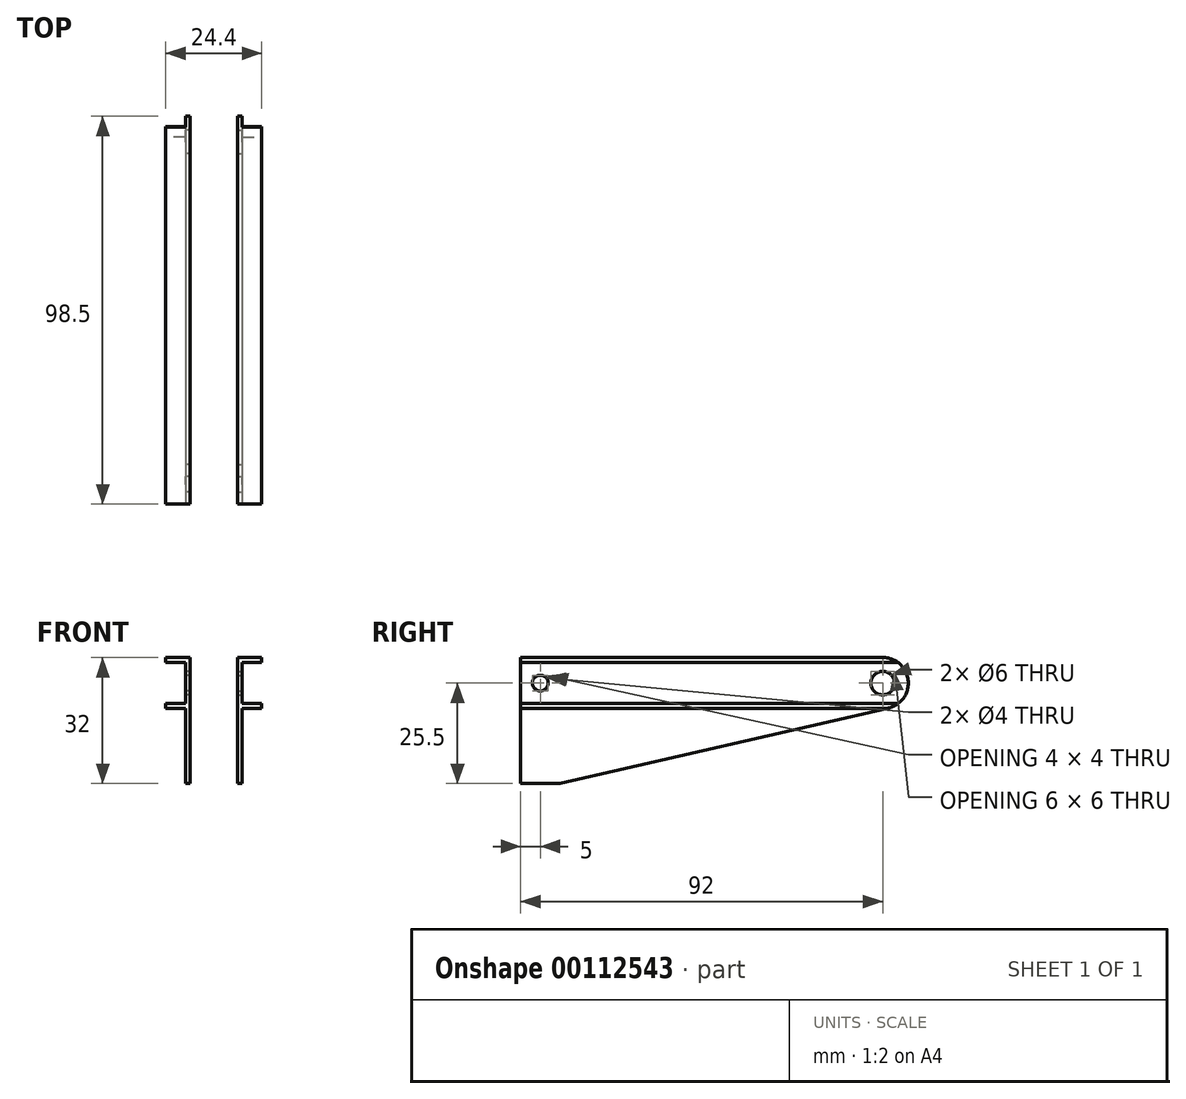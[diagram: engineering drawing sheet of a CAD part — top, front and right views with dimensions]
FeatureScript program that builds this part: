
annotation { "Feature Type Name" : "Feature", "Feature Type Description" : "" }
export const myFeature = defineFeature(function(context is Context, id is Id, definition is map)
    precondition{}
    {
        {
            var Q0;
            Q0=qCreatedBy(makeId("Front.planeOp"),FACE);
            var sketch = newSketch(context, id + "F0", { "sketchPlane" : qUnion([Q0])});
            skLineSegment(sketch, "E0", {"start": v(0, 0) * mm, "end": v(0, 16) * mm});
            skLineSegment(sketch, "E1", {"start": v(0, 16) * mm, "end": v(1.2, 16) * mm});
            skLineSegment(sketch, "E2", {"start": v(1.2, 16) * mm, "end": v(1.2, 16) * mm});
            skLineSegment(sketch, "E3", {"start": v(1.2, 16) * mm, "end": v(6.2, 16) * mm});
            skLineSegment(sketch, "E4", {"start": v(6.2, 16) * mm, "end": v(6.2, 14.8) * mm});
            skLineSegment(sketch, "E5", {"start": v(6.2, 14.8) * mm, "end": v(1.2, 14.8) * mm});
            skLineSegment(sketch, "E6", {"start": v(1.2, 14.8) * mm, "end": v(1.2, 4.3) * mm});
            skLineSegment(sketch, "E7", {"start": v(1.2, 4.3) * mm, "end": v(6.2, 4.3) * mm});
            skLineSegment(sketch, "E8", {"start": v(6.2, 4.3) * mm, "end": v(6.2, 3.1) * mm});
            skLineSegment(sketch, "E9", {"start": v(6.2, 3.1) * mm, "end": v(1.2, 3.1) * mm});
            skLineSegment(sketch, "E10", {"start": v(0, 0) * mm, "end": v(0, -16) * mm});
            skLineSegment(sketch, "E11", {"start": v(0, -16) * mm, "end": v(1.2, -16) * mm});
            skLineSegment(sketch, "E12", {"start": v(1.2, -16) * mm, "end": v(1.2, 3.1) * mm});
            skSolve(sketch);
        }
        {
            var Q0;
            Q0=makeQuery(id+"F0.imprint","IMPRINT",FACE,{"disambiguationData":[TD([[makeQuery(id+"F0.imprint","IMPRINT",EDGE,{"derivedFrom":sQuery(id+"F0.wireOp",EDGE,"E0")}),-1.0]])]});
            extrude(context, id + "F1", {"entities" : qUnion([Q0]), "oppositeDirection" : true, "depth" : 100 * mm});
        }
        {
            var Q0;
            Q0=makeQuery(id+"F1.opExtrude","SWEPT_FACE",FACE,{"disambiguationData":[OSD([sQuery(id+"F0.wireOp",EDGE,"E2")])]});
            var Q1;
            Q1=makeQuery(id+"F1.opExtrude","SWEPT_FACE",FACE,{"disambiguationData":[OSD([sQuery(id+"F0.wireOp",EDGE,"E6")])]});
            cPlane(context, id + "F2", {"entities" : qUnion([Q0, Q1]), "cplaneType" : CPlaneType.OFFSET, "offset" : 0 * mm, "width" : 150 * mm, "height" : 150 * mm});
        }
        {
            var Q0;
            Q0=qCreatedBy(id+"F2.planeOp",FACE);
            var sketch = newSketch(context, id + "F3", { "sketchPlane" : qUnion([Q0])});
            skCircle(sketch, "E13", {"center": v(5, 9.5) * mm, "radius": 2 * mm});
            skCircle(sketch, "E14.MirrorC", {"center": v(5, -10.5) * mm, "radius": 2 * mm});
            skLineSegment(sketch, "E15", {"start": v(100, 16) * mm, "end": v(100, 16) * mm});
            skCircle(sketch, "E16", {"center": v(5, 9.5) * mm, "radius": 5 * mm});
            skCircle(sketch, "E17", {"center": v(92, 9.5) * mm, "radius": 3 * mm});
            skLineSegment(sketch, "E18", {"start": v(93.45, 3.16) * mm, "end": v(10, -16) * mm});
            skArc(sketch, "E19", {"start": v(93.45, 3.16) * mm, "mid": v(98.46, 10.23) * mm, "end": v(92, 16) * mm});
            skLineSegment(sketch, "E20", {"start": v(92, 16) * mm, "end": v(100, 16) * mm});
            skLineSegment(sketch, "E21", {"start": v(100, 16) * mm, "end": v(100, -16) * mm});
            skLineSegment(sketch, "E22", {"start": v(100, -16) * mm, "end": v(10, -16) * mm});
            skSolve(sketch);
        }
        {
            var Q0;
            Q0=makeQuery(id+"F3.imprint","IMPRINT",FACE,{"disambiguationData":[TD([[makeQuery(id+"F3.imprint","IMPRINT",EDGE,{"derivedFrom":sQuery(id+"F3.wireOp",EDGE,"E14.MirrorC")}),-1.0]])]});
            var Q1;
            Q1=makeQuery(id+"F3.imprint","IMPRINT",FACE,{"disambiguationData":[TD([[makeQuery(id+"F3.imprint","IMPRINT",EDGE,{"derivedFrom":sQuery(id+"F3.wireOp",EDGE,"E13")}),1.0]])]});
            var Q2;
            Q2=makeQuery(id+"F3.imprint","IMPRINT",FACE,{"disambiguationData":[TD([[makeQuery(id+"F3.imprint","IMPRINT",EDGE,{"derivedFrom":sQuery(id+"F3.wireOp",EDGE,"574HhtLP-nTTJ-pekG-s0HU-Gk7TssawcMeE")}),-1.0]])]});
            var Q3;
            Q3=makeQuery(id+"F3.imprint","IMPRINT",FACE,{"disambiguationData":[TD([[makeQuery(id+"F3.imprint","IMPRINT",EDGE,{"derivedFrom":sQuery(id+"F3.wireOp",EDGE,"buxoA0jU-tP47-w18K-Fbsk-EydC5CnxEHID")}),1.0]])]});
            var Q4;
            Q4=makeQuery(id+"F3.imprint","IMPRINT",FACE,{"disambiguationData":[TD([[makeQuery(id+"F3.imprint","IMPRINT",EDGE,{"derivedFrom":sQuery(id+"F3.wireOp",EDGE,"E17")}),1.0]])]});
            var Q5;
            {var subQ0=sQuery(id+"F3.wireOp",EDGE,"CZpuG06R-nE2b-Nvu3-mtoJ-QHwZorgtmSJN");Q5=makeQuery(id+"F3.imprint","IMPRINT",FACE,{"disambiguationData":[TD([[makeQuery(id+"F3.imprint","IMPRINT",EDGE,{"derivedFrom":subQ0}),-1.0]])]});}
            var Q6;
            {var subQ0=sQuery(id+"F3.wireOp",EDGE,"xbh0oJhC-akQt-KU1N-uazl-jcToiNu8Anxt");Q6=makeQuery(id+"F3.imprint","IMPRINT",FACE,{"disambiguationData":[TD([[makeQuery(id+"F3.imprint","IMPRINT",EDGE,{"derivedFrom":subQ0}),1.0]])]});}
            var Q7;
            Q7=makeQuery(id+"F3.imprint","IMPRINT",FACE,{"disambiguationData":[TD([[makeQuery(id+"F3.imprint","IMPRINT",EDGE,{"derivedFrom":sQuery(id+"F3.wireOp",EDGE,"E18")}),1.0]])]});
            extrude(context, id + "F4", {"entities" : qUnion([Q0, Q1, Q2, Q3, Q4, Q5, Q6, Q7]), "operationType" : NewBodyOperationType.REMOVE, "endBound" : BoundingType.SYMMETRIC, "oppositeDirection" : true, "depth" : 25 * mm});
        }
        {
            var Q0;
            Q0=makeQuery(id+"F1.opExtrude","SWEPT_BODY",BODY,{"disambiguationData":[OSD([sQuery(id+"F0.wireOp",EDGE,"E0"),sQuery(id+"F0.wireOp",EDGE,"E1"),sQuery(id+"F0.wireOp",EDGE,"E2"),sQuery(id+"F0.wireOp",EDGE,"E3"),sQuery(id+"F0.wireOp",EDGE,"E4"),sQuery(id+"F0.wireOp",EDGE,"E5"),sQuery(id+"F0.wireOp",EDGE,"E6"),sQuery(id+"F0.wireOp",EDGE,"E7"),sQuery(id+"F0.wireOp",EDGE,"E8"),sQuery(id+"F0.wireOp",EDGE,"E9"),sQuery(id+"F0.wireOp",EDGE,"E10"),sQuery(id+"F0.wireOp",EDGE,"E11"),sQuery(id+"F0.wireOp",EDGE,"E12")])]});
            transform(context, id + "F5", {"entities" : qUnion([Q0]), "transformType" : TransformType.TRANSLATION_3D, "dx" : 6 * mm, "dy" : 0 * mm, "dz" : 0 * mm, "makeCopy" : false});
        }
        {
            var Q0;
            Q0=makeQuery(id+"F1.opExtrude","SWEPT_BODY",BODY,{"disambiguationData":[OSD([sQuery(id+"F0.wireOp",EDGE,"E0"),sQuery(id+"F0.wireOp",EDGE,"E1"),sQuery(id+"F0.wireOp",EDGE,"E2"),sQuery(id+"F0.wireOp",EDGE,"E3"),sQuery(id+"F0.wireOp",EDGE,"E4"),sQuery(id+"F0.wireOp",EDGE,"E5"),sQuery(id+"F0.wireOp",EDGE,"E6"),sQuery(id+"F0.wireOp",EDGE,"E7"),sQuery(id+"F0.wireOp",EDGE,"E8"),sQuery(id+"F0.wireOp",EDGE,"E9"),sQuery(id+"F0.wireOp",EDGE,"E10"),sQuery(id+"F0.wireOp",EDGE,"E11"),sQuery(id+"F0.wireOp",EDGE,"E12")])]});
            var Q1;
            Q1=qCreatedBy(makeId("Right.planeOp"),FACE);
            mirror(context, id + "F6", {"entities" : qUnion([Q0]), "mirrorPlane" : qUnion([Q1])});
        }
    });
